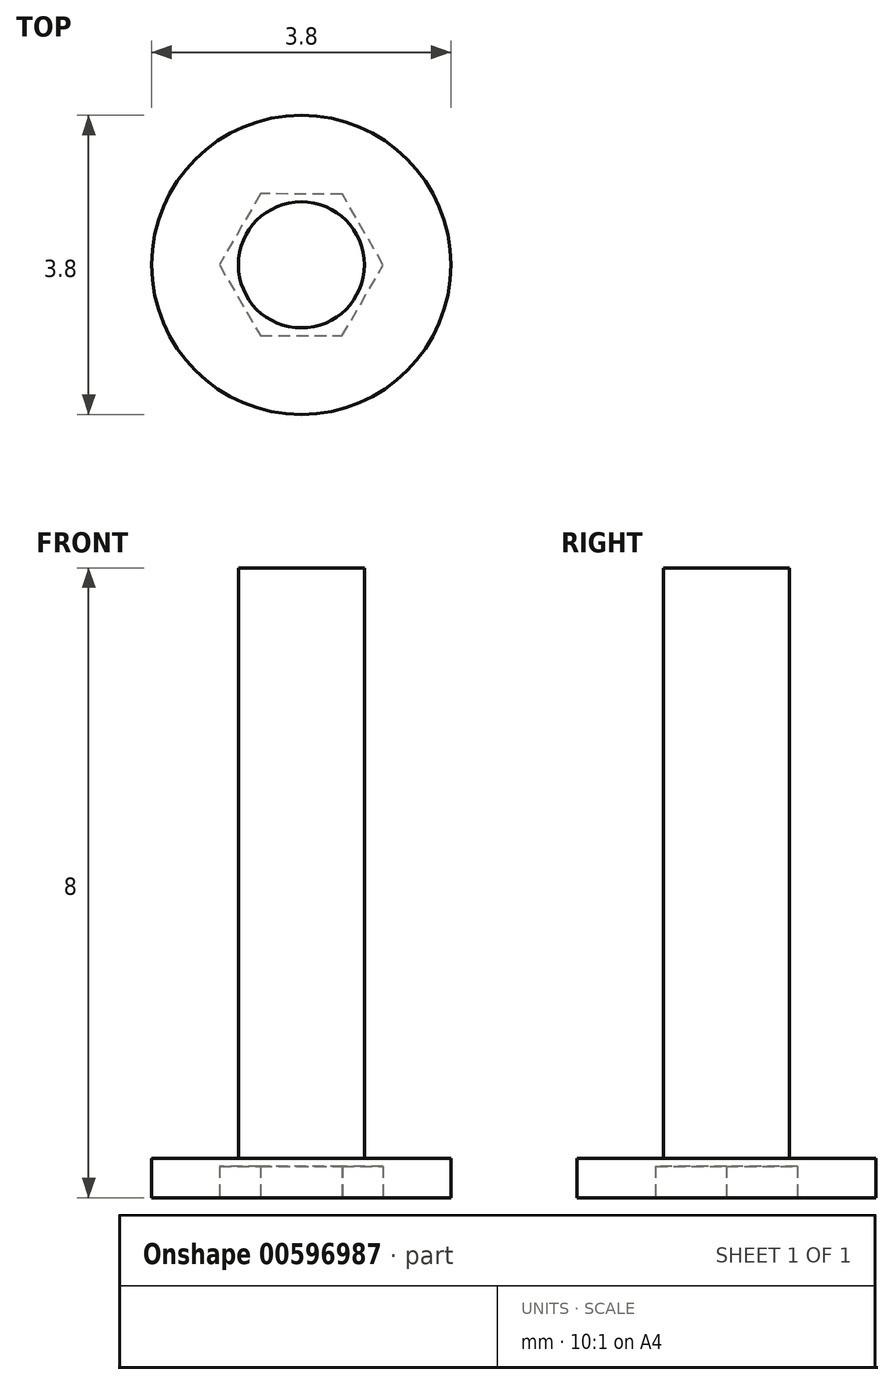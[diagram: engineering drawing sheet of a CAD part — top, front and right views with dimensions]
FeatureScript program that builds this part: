
annotation { "Feature Type Name" : "Feature", "Feature Type Description" : "" }
export const myFeature = defineFeature(function(context is Context, id is Id, definition is map)
    precondition{}
    {
        {
            var Q0;
            Q0=qCreatedBy(makeId("Top.planeOp"),FACE);
            var sketch = newSketch(context, id + "F0", { "sketchPlane" : qUnion([Q0])});
            skCircle(sketch, "E0", {"center": v(0, 0) * mm, "radius": 1.9 * mm});
            skCircle(sketch, "E1", {"center": v(0, 0) * mm, "radius": 0.8 * mm});
            skPoint(sketch, "E2.0.midPoint", {"position": v(0.76, 0.45) * mm});
            skSolve(sketch);
        }
        {
            var Q0;
            Q0=makeQuery(id+"F0.imprint","IMPRINT",FACE,{"disambiguationData":[TD([[makeQuery(id+"F0.imprint","IMPRINT",EDGE,{"derivedFrom":sQuery(id+"F0.wireOp",EDGE,"E1")}),1.0]])]});
            extrude(context, id + "F1", {"entities" : qUnion([Q0]), "depth" : 8 * mm});
        }
        {
            var Q0;
            Q0=makeQuery(id+"F0.imprint","IMPRINT",FACE,{"disambiguationData":[TD([[makeQuery(id+"F0.imprint","IMPRINT",EDGE,{"derivedFrom":sQuery(id+"F0.wireOp",EDGE,"E0")}),1.0]])]});
            extrude(context, id + "F2", {"entities" : qUnion([Q0]), "operationType" : NewBodyOperationType.ADD, "depth" : 0.5 * mm});
        }
        {
            var Q0;
            {var subQ0=sQuery(id+"F0.wireOp",EDGE,"E1");Q0=makeQuery(id+"F2.boolean.opBoolean","MERGE",FACE,{"derivedFrom":[makeQuery(id+"F1.opExtrude","CAP_FACE",FACE,{"disambiguationData":[OSD([subQ0])],"isStart":true}),makeQuery(id+"F2.opExtrude","CAP_FACE",FACE,{"disambiguationData":[OSD([sQuery(id+"F0.wireOp",EDGE,"E0"),subQ0])],"isStart":true})]});}
            var sketch = newSketch(context, id + "F3", { "sketchPlane" : qUnion([Q0])});
            skCircle(sketch, "E3.cCircle", {"center": v(0, 0) * mm, "radius": 0.9 * mm, "construction": true});
            skLineSegment(sketch, "E3.0", {"start": v(1.04, 0) * mm, "end": v(0.52, -0.9) * mm});
            skLineSegment(sketch, "E3.1", {"start": v(0.52, -0.9) * mm, "end": v(-0.52, -0.9) * mm});
            skLineSegment(sketch, "E3.2", {"start": v(-0.52, -0.9) * mm, "end": v(-1.04, 0) * mm});
            skLineSegment(sketch, "E3.3", {"start": v(-1.04, 0) * mm, "end": v(-0.52, 0.9) * mm});
            skLineSegment(sketch, "E3.4", {"start": v(-0.52, 0.9) * mm, "end": v(0.52, 0.9) * mm});
            skLineSegment(sketch, "E3.5", {"start": v(0.52, 0.9) * mm, "end": v(1.04, 0) * mm});
            skPoint(sketch, "E3.0.midPoint", {"position": v(0.78, -0.45) * mm});
            skSolve(sketch);
        }
        {
            var Q0;
            Q0=makeQuery(id+"F3.imprint","IMPRINT",FACE,{"disambiguationData":[TD([[makeQuery(id+"F3.imprint","IMPRINT",EDGE,{"derivedFrom":sQuery(id+"F3.wireOp",EDGE,"E3.0")}),-1.0]])]});
            extrude(context, id + "F4", {"entities" : qUnion([Q0]), "operationType" : NewBodyOperationType.REMOVE, "oppositeDirection" : true, "depth" : 0.4 * mm});
        }
    });
